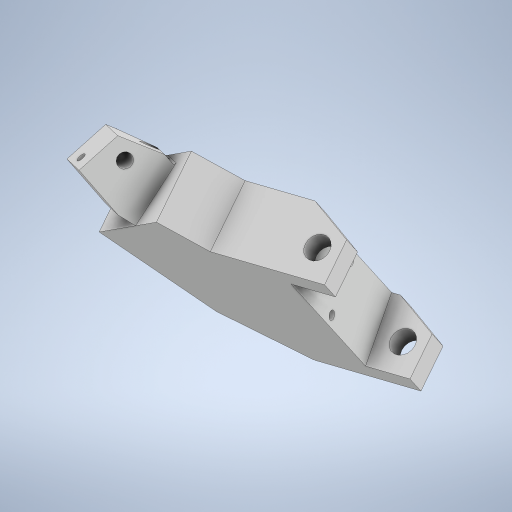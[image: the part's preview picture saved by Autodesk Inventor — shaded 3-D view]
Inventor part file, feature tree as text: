
AUTODESK INVENTOR PART (.ipt)
format: ipt  version: 2024 (Build 280153000, 153)  size: 381,952 bytes
history: native  units: in
note: dims shown in document units (in); Inventor stores cm internally (conversion verified against a paired STEP export)
features: other x3, extrude x2, sketch x2, boolean_combine x1
ambient origin geometry x8: Origin, YZ Plane, XZ Plane, XY Plane, X Axis, Y Axis, Z Axis, Center Point
bodies: Solid1 (feature_tree), Solid2 (feature_tree)
feature tree (8):
  other  "lowerAssembly.iam"
  other  "lower.ipt:2"
  other  "normMale.ipt:1"
  boolean_combine  "Combine1"
  extrude  "Extrusion1"  Depth=0.3937in TaperAngle=0.0deg
  extrude  "Extrusion2"  [1 undecoded]
  sketch  "Sketch1"  dims[d1=0.3937in d2=1.0in d3=0.0in]
  sketch  "Sketch2"  dims[d4=1.0in d5=0.0in]
note: 1 required parameter value undecoded (feature->parameter linkage not recoverable at this tier; creation-order binding heuristic only, values carry confidence <= 0.55)
